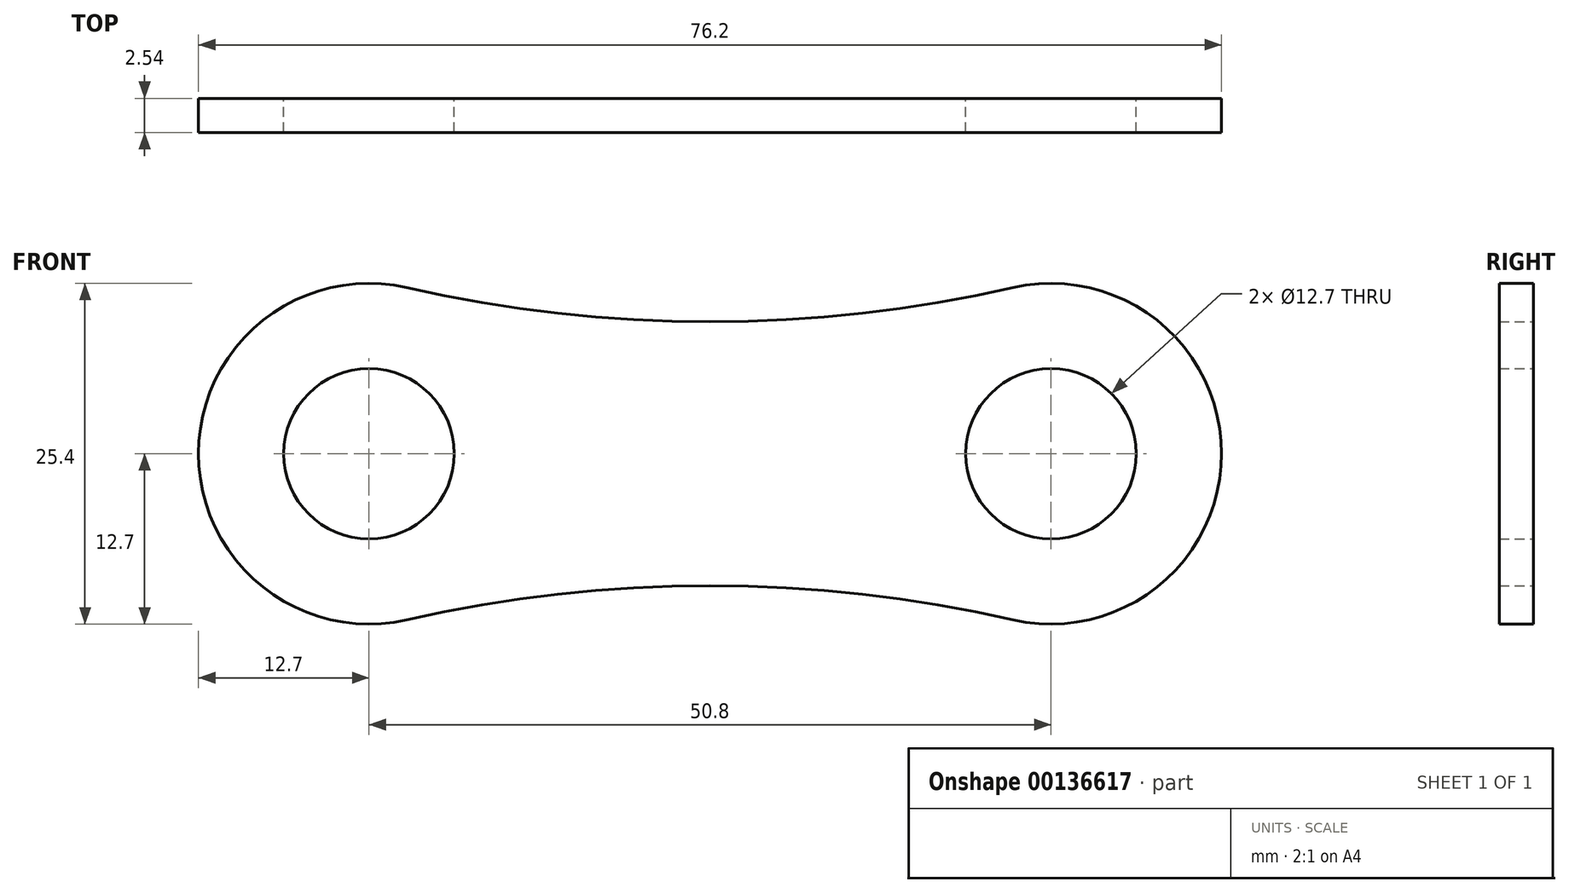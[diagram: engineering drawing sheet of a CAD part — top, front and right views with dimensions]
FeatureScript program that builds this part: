
annotation { "Feature Type Name" : "Feature", "Feature Type Description" : "" }
export const myFeature = defineFeature(function(context is Context, id is Id, definition is map)
    precondition{}
    {
        {
            var Q0;
            Q0=qCreatedBy(makeId("Front.planeOp"),FACE);
            var sketch = newSketch(context, id + "F0", { "sketchPlane" : qUnion([Q0])});
            skArc(sketch, "E0", {"start": v(22.58, 12.38) * mm, "mid": v(38.1, 0) * mm, "end": v(22.58, -12.38) * mm});
            skCircle(sketch, "E1", {"center": v(-25.4, 0) * mm, "radius": 6.35 * mm});
            skCircle(sketch, "E2", {"center": v(25.4, 0) * mm, "radius": 6.35 * mm});
            skArc(sketch, "E3", {"start": v(-22.58, 12.38) * mm, "mid": v(-38.1, 0) * mm, "end": v(-22.58, -12.38) * mm});
            skArc(sketch, "E4", {"start": v(-22.58, 12.38) * mm, "mid": v(0, 9.84) * mm, "end": v(22.58, 12.38) * mm});
            skArc(sketch, "E5", {"start": v(22.58, -12.38) * mm, "mid": v(0, -9.84) * mm, "end": v(-22.58, -12.38) * mm});
            skSolve(sketch);
        }
        {
            var Q0;
            Q0 = qSketchRegion(id + "F0", true);
            extrude(context, id + "F1", {"entities" : qUnion([Q0]), "depth" : 2.54 * mm});
        }
    });
